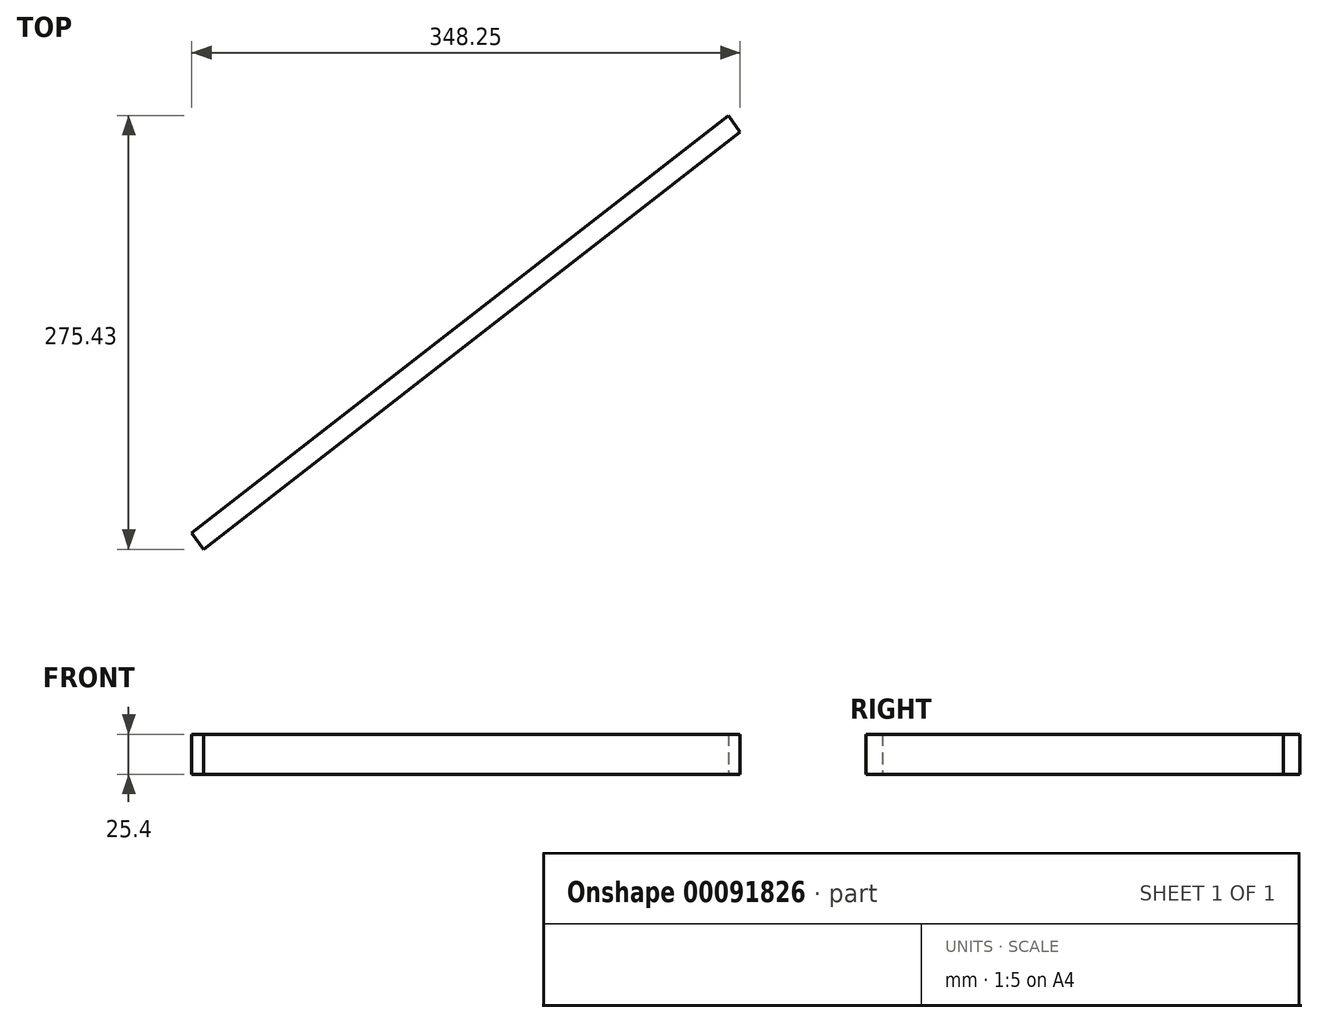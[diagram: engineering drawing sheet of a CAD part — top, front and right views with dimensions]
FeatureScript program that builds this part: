
annotation { "Feature Type Name" : "Feature", "Feature Type Description" : "" }
export const myFeature = defineFeature(function(context is Context, id is Id, definition is map)
    precondition{}
    {
        {
            var Q0;
            Q0=qCreatedBy(makeId("Top.planeOp"),FACE);
            var sketch = newSketch(context, id + "F0", { "sketchPlane" : qUnion([Q0])});
            skLineSegment(sketch, "E0", {"start": v(0, 0) * mm, "end": v(-340.82, -265.12) * mm});
            skLineSegment(sketch, "E1", {"start": v(7.43, -10.3) * mm, "end": v(-333.4, -275.43) * mm});
            skLineSegment(sketch, "E2", {"start": v(-333.4, -275.43) * mm, "end": v(-340.82, -265.12) * mm});
            skLineSegment(sketch, "E3", {"start": v(7.43, -10.3) * mm, "end": v(0, 0) * mm});
            skSolve(sketch);
        }
        {
            var Q0;
            Q0=makeQuery(id+"F0.imprint","IMPRINT",FACE,{"disambiguationData":[TD([[makeQuery(id+"F0.imprint","IMPRINT",EDGE,{"derivedFrom":sQuery(id+"F0.wireOp",EDGE,"E0")}),1.0]])]});
            extrude(context, id + "F1", {"entities" : qUnion([Q0]), "depth" : 25.4 * mm});
        }
    });
